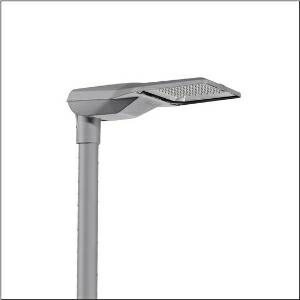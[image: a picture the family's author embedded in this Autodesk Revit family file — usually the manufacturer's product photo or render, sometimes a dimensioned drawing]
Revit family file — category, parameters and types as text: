
# Revit family: streetlight_sl_21_iq_midi___st1_0ab_5xe3m31g08nb_68e1
name_source: partatom
category: Lighting Fixtures
units: mm (PartAtom-declared; Revit-internal decimal feet)

## family parameters
Cut with Voids When Loaded = No
Host = Face
Light Source = No
Part Type = Normal
Room Calculation Point = No
Round Connector Dimension = Use Diameter
Shared = No

## types (1)
- --- (1 x LED, 20440 lm, 155.5 W, 3000K)
    Apparent Load = 155 VA
    CIE Flux Codes = 40 74 97 100 100
    Color Rendering = 70
    Color Temperature = 3000K
    Default Elevation = 1800 mm
    Description = Streetlight SL 21 iQ midi, mast luminaire, primary light control with lens, of PMMA, primary optical cover: cover, of toughened safety glass, transparent, light distribution: ST1.0aB, light emission: direct distribution, primary light characteristic: asymmetric, installation type: post-top, side-entry, LED, High Power LED, rated luminous flux: 20.440lm, luminous efficacy: 131lm/W, light colour: 730, colour temperature: 3000K, control gear: iQ Street-Remote, control: Street-Remote, Auto-Match, Temp-Guard, Lumen-Switch, Night-Set, Smart-Wire, Light-Fading, Desk-Remote (wireless, voltage-free reading and setting of iQ features in the workshop via application-optimized NFC function/RFID function), optimised constant luminous flux control (CLO 2.0), pre-setting: linear dimming characteristic, mains connection: 230..240V, AC, 50/60Hz, start of lifetime: 156W, end of service life: 162W, reduction: 69W, luminaire housing, of diecast aluminium, powder-coated, Siteco® metallic grey (DB 702S), corrosivity category C5 mid according to DIN EN ISO 12944, please order mast flange separately, inclination adjustable: 0°, 5°, 10°, 15°, sealing non-destructively replaceable, multi-level sealing system, length: 644mm, width: 335mm, height: 110mm, mast flange for spigot size: 42mm (side-entry): 5XC10008XM4, 60/48mm (side-entry/post-top): 5XC10108XM2, 76/60mm (side-entry/post-top): 5XC10108XM1, mounting height: 4..8m, protection rating (complete): IP66, insulation class (complete): insulation class II (safety insulation), certification: CE, ENEC, ENEC+, VDE, impact resistance: IK10, permissible operating ambient temperature for outdoor applications: -40..+50°C, standard-compliant lighting for roads and squares, packaging unit: 1 piece

Light Distribution: ST1.0aB
    Height = 111 mm
    Lamp = 1 x LED
    Lamp Light Flux = 20440 lm
    Lamp Power = 155.5 W
    Lamp count = 1
    Length = 644 mm
    Luminous efficacy = 131 lm/W
    Manufacturer = Siteco
    ModVariant = No
    Model = 5XE3M31G08NB
    Number of Poles = 1
    OnlyDefault = Yes
    Power Factor = 1
    Product Name = Streetlight SL 21 iQ midi | ST1.0aB
    Product group = mast luminaire | pylon top
    ProductGroupID = 6100
    Protection Class = Protection class II
    Protection Degree = IP 66
    RLX_Detail_Level = 1
    RLX_Emergency_Light_Flux = 0 lm
    RLX_Emergency_Type = 0
    RLX_Emergency_Type_DB = No
    RlxData = <blob elided: 27169 chars, md5=c19c5daa>
    Socket = socket
    Standby Power = 0 W
    System Light Flux = 20440 lm
    System Power = 155 W
    Type Comments = factory setting: luminous flux: 100 % | dim-lin: 254 | 823 mA
    Type Image = l_1004298.jpg
    URL = http://relux.com
    VarID = @adj_168222
    Voltage = 0 V
    Weight = 0.00 kg
    Width = 336 mm

## geometry (parser evidence)
native form markers: Blend x4, Sweep x10
no freeform markers — native parametric forms only
